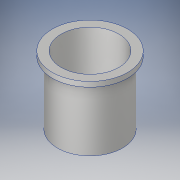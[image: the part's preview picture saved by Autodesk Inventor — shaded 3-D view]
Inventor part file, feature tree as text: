
AUTODESK INVENTOR PART (.ipt)
format: ipt  version: 2017 SP1 (Build 210196100, 196)  size: 154,624 bytes
history: native  units: in
note: dims shown in document units (in); Inventor stores cm internally (conversion verified against a paired STEP export)
features: revolve x1, sketch x1
ambient origin geometry x8: Origin, YZ Plane, XZ Plane, XY Plane, X Axis, Y Axis, Z Axis, Center Point
bodies: Solid1 (feature_tree)
feature tree (2):
  revolve  "Revolution1"  [1 undecoded]
  sketch  "Sketch1"  dims[d0=0.5in d1=1.13in d3=15.0deg d4=0.25in d9=1.5in d11=0.5in d13=3.75in d14=0.25in d15=1.0in d16=0.25in d17=0.5in d18=0.234in d19=0.234in d20=0.5in d22=4.25in d23=2.5in d25=1.0in d26=0.25in d27=5.25in d28=0.125in d29=4.0in d30=0.25in d31=0.1718in d32=1.75in d33=0.125in d34=0.801in d35=0.375in d37=90.0deg]
note: 1 required parameter value undecoded (feature->parameter linkage not recoverable at this tier; creation-order binding heuristic only, values carry confidence <= 0.55)
